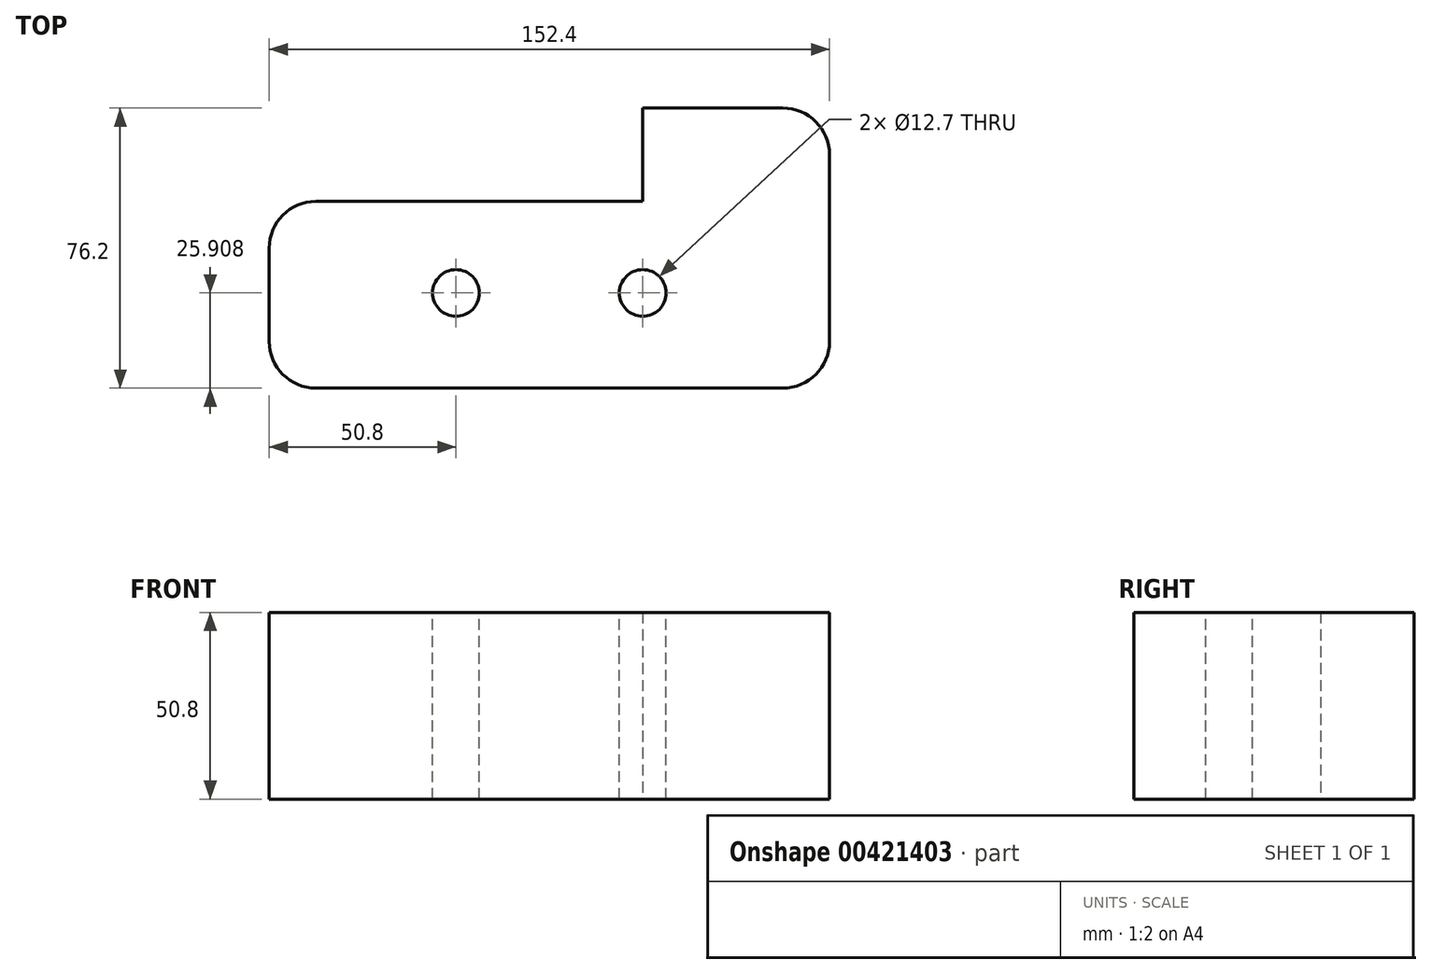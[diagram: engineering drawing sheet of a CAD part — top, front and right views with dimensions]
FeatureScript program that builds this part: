
annotation { "Feature Type Name" : "Feature", "Feature Type Description" : "" }
export const myFeature = defineFeature(function(context is Context, id is Id, definition is map)
    precondition{}
    {
        {
            var Q0;
            Q0=qCreatedBy(makeId("Top.planeOp"),FACE);
            var sketch = newSketch(context, id + "F0", { "sketchPlane" : qUnion([Q0])});
            skLineSegment(sketch, "E0", {"start": v(0, 0) * mm, "end": v(152.4, 0) * mm});
            skLineSegment(sketch, "E1", {"start": v(0, 0) * mm, "end": v(0, 50.8) * mm});
            skLineSegment(sketch, "E2", {"start": v(0, 50.8) * mm, "end": v(101.6, 50.8) * mm});
            skLineSegment(sketch, "E3", {"start": v(101.6, 50.8) * mm, "end": v(101.6, 76.2) * mm});
            skLineSegment(sketch, "E4", {"start": v(101.6, 76.2) * mm, "end": v(152.4, 76.2) * mm});
            skLineSegment(sketch, "E5", {"start": v(152.4, 76.2) * mm, "end": v(152.4, 0) * mm});
            skSolve(sketch);
        }
        {
            var Q0;
            Q0 = qSketchRegion(id + "F0", true);
            extrude(context, id + "F1", {"entities" : qUnion([Q0]), "depth" : 50.8 * mm});
        }
        {
            var Q0;
            Q0=makeQuery(id+"F1.opExtrude","SWEPT_EDGE",EDGE,{"disambiguationData":[OSD([sQuery(id+"F0.wireOp",EDGE,"E4"),sQuery(id+"F0.wireOp",EDGE,"E5")])]});
            var Q1;
            Q1=makeQuery(id+"F1.opExtrude","SWEPT_EDGE",EDGE,{"disambiguationData":[OSD([sQuery(id+"F0.wireOp",EDGE,"E0"),sQuery(id+"F0.wireOp",EDGE,"E5")])]});
            var Q2;
            Q2=makeQuery(id+"F1.opExtrude","SWEPT_EDGE",EDGE,{"disambiguationData":[OSD([sQuery(id+"F0.wireOp",EDGE,"E0"),sQuery(id+"F0.wireOp",EDGE,"E1")])]});
            var Q3;
            Q3=makeQuery(id+"F1.opExtrude","SWEPT_EDGE",EDGE,{"disambiguationData":[OSD([sQuery(id+"F0.wireOp",EDGE,"E1"),sQuery(id+"F0.wireOp",EDGE,"E2")])]});
            fillet(context, id + "F2", {"entities" : qUnion([Q0, Q1, Q2, Q3]), "radius" : 12.7 * mm, "tangentPropagation" : true, "allowEdgeOverflow" : false});
        }
        {
            var Q0;
            Q0=makeQuery(id+"F1.opExtrude","CAP_FACE",FACE,{"disambiguationData":[OSD([sQuery(id+"F0.wireOp",EDGE,"E0"),sQuery(id+"F0.wireOp",EDGE,"E1"),sQuery(id+"F0.wireOp",EDGE,"E2"),sQuery(id+"F0.wireOp",EDGE,"E3"),sQuery(id+"F0.wireOp",EDGE,"E4"),sQuery(id+"F0.wireOp",EDGE,"E5")])],"isStart":false});
            var sketch = newSketch(context, id + "F3", { "sketchPlane" : qUnion([Q0])});
            skPoint(sketch, "E6", {"position": v(0, 25.4) * mm});
            skPoint(sketch, "E7", {"position": v(50.8, 25.9) * mm});
            skPoint(sketch, "E8", {"position": v(101.6, 25.9) * mm});
            skSolve(sketch);
        }
        {
            var Q0;
            Q0=sQuery(id+"F3.wireOp",VERTEX,"E7");
            var Q1;
            Q1=sQuery(id+"F3.wireOp",VERTEX,"E8");
            var Q2;
            Q2=makeQuery(id+"F1.opExtrude","SWEPT_BODY",BODY,{"disambiguationData":[OSD([sQuery(id+"F0.wireOp",EDGE,"E0"),sQuery(id+"F0.wireOp",EDGE,"E1"),sQuery(id+"F0.wireOp",EDGE,"E2"),sQuery(id+"F0.wireOp",EDGE,"E3"),sQuery(id+"F0.wireOp",EDGE,"E4"),sQuery(id+"F0.wireOp",EDGE,"E5")])]});
            hole(context, id + "F4", {"style" : HoleStyle.SIMPLE, "endStyle" : HoleEndStyle.THROUGH, "holeDiameter" : 12.7 * mm, "isTappedThrough" : true, "tappedDepth" : 12.7 * mm, "tapClearance" : 3, "locations" : qUnion([Q0, Q1]), "scope" : qUnion([Q2])});
        }
    });
